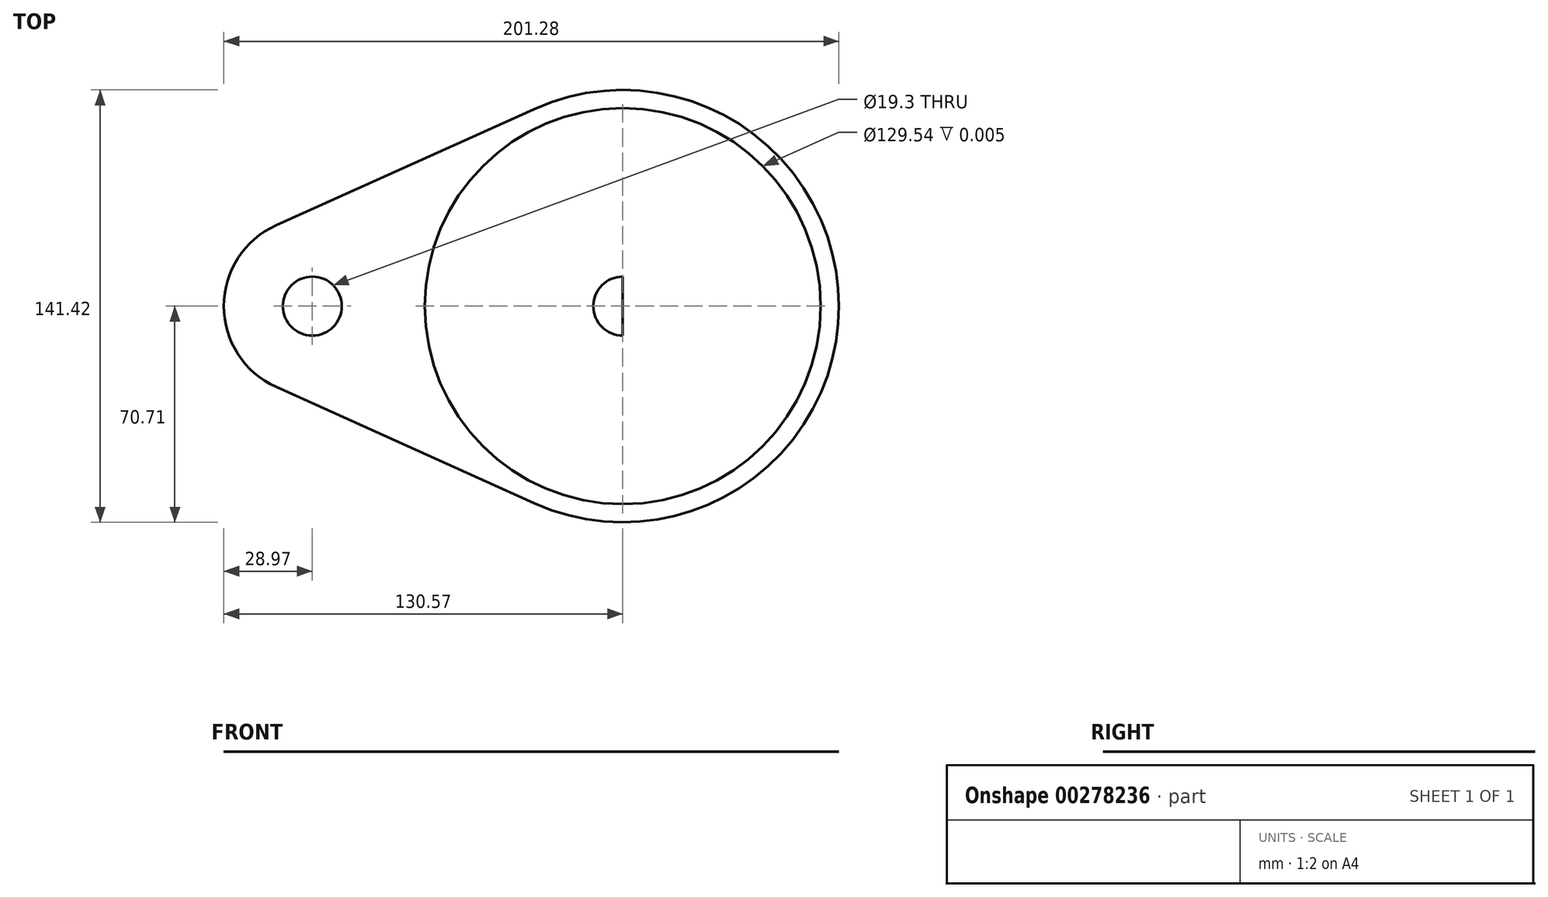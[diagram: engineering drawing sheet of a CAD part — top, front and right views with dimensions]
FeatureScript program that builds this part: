
annotation { "Feature Type Name" : "Feature", "Feature Type Description" : "" }
export const myFeature = defineFeature(function(context is Context, id is Id, definition is map)
    precondition{}
    {
        {
            var Q0;
            Q0=qCreatedBy(makeId("Top.planeOp"),FACE);
            var sketch = newSketch(context, id + "F0", { "sketchPlane" : qUnion([Q0])});
            skCircle(sketch, "E0", {"center": v(0, 0) * mm, "radius": 64.77 * mm});
            skLineSegment(sketch, "E1", {"start": v(0, 0) * mm, "end": v(-101.6, 0) * mm});
            skCircle(sketch, "E2", {"center": v(-101.6, 0) * mm, "radius": 13.9 * mm});
            skArc(sketch, "E3", {"start": v(-113.5, 26.41) * mm, "mid": v(-130.57, 0) * mm, "end": v(-113.5, -26.41) * mm});
            skArc(sketch, "E4", {"start": v(-29.05, -64.46) * mm, "mid": v(70.7, 0) * mm, "end": v(-29.05, 64.46) * mm});
            skLineSegment(sketch, "E5", {"start": v(-113.5, 26.41) * mm, "end": v(-29.05, 64.46) * mm});
            skLineSegment(sketch, "E6", {"start": v(-113.5, -26.41) * mm, "end": v(-29.05, -64.46) * mm});
            skLineSegment(sketch, "E7", {"start": v(0, 64.77) * mm, "end": v(0, -64.77) * mm});
            skPoint(sketch, "E8.MirrorCS.end.orphan", {"position": v(29.05, 64.46) * mm});
            skPoint(sketch, "E8.MirrorCS.start.orphan", {"position": v(113.5, 26.41) * mm});
            skPoint(sketch, "E9.MirrorCS.end.orphan", {"position": v(113.5, -26.41) * mm});
            skPoint(sketch, "E10.MirrorCS.end.orphan", {"position": v(29.05, -64.46) * mm});
            skCircle(sketch, "E11", {"center": v(-101.6, 0) * mm, "radius": 9.65 * mm});
            skCircle(sketch, "E12", {"center": v(0, 0) * mm, "radius": 9.65 * mm});
            skSolve(sketch);
        }
        {
            var Q0;
            Q0=makeQuery(id+"F0.imprint","IMPRINT",FACE,{"disambiguationData":[TD([[makeQuery(id+"F0.imprint","IMPRINT",EDGE,{"derivedFrom":sQuery(id+"F0.wireOp",EDGE,"E2")}),-1.0]])]});
            var Q1;
            Q1=makeQuery(id+"F0.imprint","IMPRINT",FACE,{"disambiguationData":[TD([[makeQuery(id+"F0.imprint","IMPRINT",EDGE,{"derivedFrom":sQuery(id+"F0.wireOp",EDGE,"E2")}),1.0]])]});
            var Q2;
            {var subQ0=sQuery(id+"F0.wireOp",EDGE,"E0");var subQ1=sQuery(id+"F0.wireOp",EDGE,"E1");var subQ2=makeQuery(id+"F0.imprint","INTERSECT",VERTEX,{"derivedFrom":[subQ1,subQ0]});Q2=makeQuery(id+"F0.imprint","IMPRINT",FACE,{"disambiguationData":[TD([[makeQuery(id+"F0.imprint","IMPRINT",EDGE,{"disambiguationData":[TD([[subQ2,1.0]])],"derivedFrom":subQ1}),-1.0]])]});}
            var Q3;
            {var subQ0=sQuery(id+"F0.wireOp",EDGE,"E0");var subQ1=sQuery(id+"F0.wireOp",EDGE,"E1");var subQ2=makeQuery(id+"F0.imprint","INTERSECT",VERTEX,{"derivedFrom":[subQ1,subQ0]});Q3=makeQuery(id+"F0.imprint","IMPRINT",FACE,{"disambiguationData":[TD([[makeQuery(id+"F0.imprint","IMPRINT",EDGE,{"disambiguationData":[TD([[subQ2,1.0]])],"derivedFrom":subQ1}),1.0]])]});}
            var Q4;
            {var subQ0=sQuery(id+"F0.wireOp",EDGE,"E0");var subQ1=sQuery(id+"F0.wireOp",EDGE,"E7");var subQ2=makeQuery(id+"F0.imprint","INTERSECT",VERTEX,{"disambiguationData":[OD(0.0)],"derivedFrom":[subQ1,subQ0]});Q4=makeQuery(id+"F0.imprint","IMPRINT",FACE,{"disambiguationData":[TD([[makeQuery(id+"F0.imprint","IMPRINT",EDGE,{"disambiguationData":[TD([[subQ2,-1.0]])],"derivedFrom":subQ1}),1.0]])]});}
            extrude(context, id + "F1", {"entities" : qUnion([Q0, Q1, Q2, Q3, Q4]), "depth" : 1 / 203.2 * mm});
        }
    });
